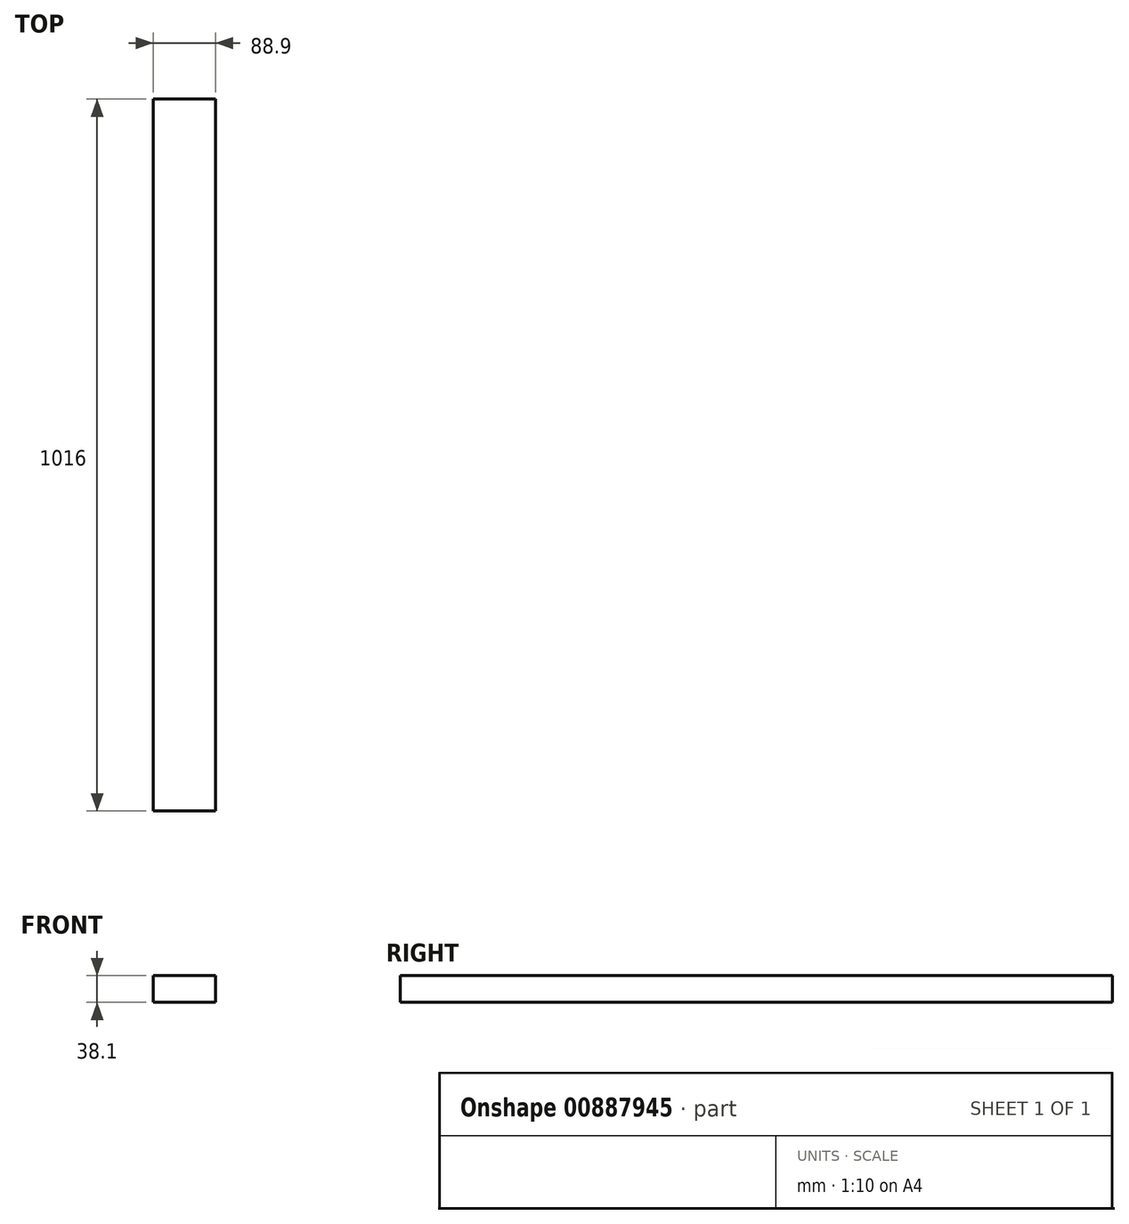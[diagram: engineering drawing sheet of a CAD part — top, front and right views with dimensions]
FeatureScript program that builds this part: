
annotation { "Feature Type Name" : "Feature", "Feature Type Description" : "" }
export const myFeature = defineFeature(function(context is Context, id is Id, definition is map)
    precondition{}
    {
        {
            var Q0;
            Q0=qCreatedBy(makeId("Front.planeOp"),FACE);
            var sketch = newSketch(context, id + "F0", { "sketchPlane" : qUnion([Q0])});
            skLineSegment(sketch, "E0.bottom", {"start": v(44.45, -19.05) * mm, "end": v(-44.45, -19.05) * mm});
            skLineSegment(sketch, "E0.top", {"start": v(44.45, 19.05) * mm, "end": v(-44.45, 19.05) * mm});
            skLineSegment(sketch, "E0.left", {"start": v(44.45, -19.05) * mm, "end": v(44.45, 19.05) * mm});
            skLineSegment(sketch, "E0.right", {"start": v(-44.45, -19.05) * mm, "end": v(-44.45, 19.05) * mm});
            skPoint(sketch, "E0.middle", {"position": v(0, 0) * mm});
            skSolve(sketch);
        }
        {
            var Q0;
            Q0=qSketchRegion(id+"F0",true);
            extrude(context, id + "F1", {"entities" : qUnion([Q0]), "depth" : 1016 * mm, "offsetDistance" : 25.4 * mm});
        }
    });
